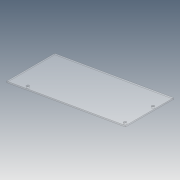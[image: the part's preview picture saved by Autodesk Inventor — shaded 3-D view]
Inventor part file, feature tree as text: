
AUTODESK INVENTOR PART (.ipt)
format: ipt  version: 2012 (Build 160160000, 160)  size: 78,848 bytes
history: native  units: in
note: dims shown in document units (in); Inventor stores cm internally (conversion verified against a paired STEP export)
features: pattern_linear x2, extrude x1, hole x1, sketch x1, reference x1
ambient origin geometry x8: Origin, YZ Plane, XZ Plane, XY Plane, X Axis, Y Axis, Z Axis, Center Point
bodies: Solid1 (feature_tree)
feature tree (6):
  extrude  "Extrusion1"  Depth=0.7874in
  hole  "Hole1"  [1 undecoded]
  pattern_linear  "Rectangular Pattern1"  [2 undecoded]
  pattern_linear  "Rectangular Pattern2"  [2 undecoded]
  sketch  "Sketch1"  dims[d0=4.625in d1=0.0in d2=0.375in d3=0.3125in d4=0.265in d5=0.75in d6=0.375in d7=0.25in d8=0.5635in d9=1.0in d10=0.8108in d11=0.7874in d13=9.5in d14=0.7874in d16=2.6875in]
  reference  "Reference1"
note: 5 required parameter values undecoded (feature->parameter linkage not recoverable at this tier; creation-order binding heuristic only, values carry confidence <= 0.55)
